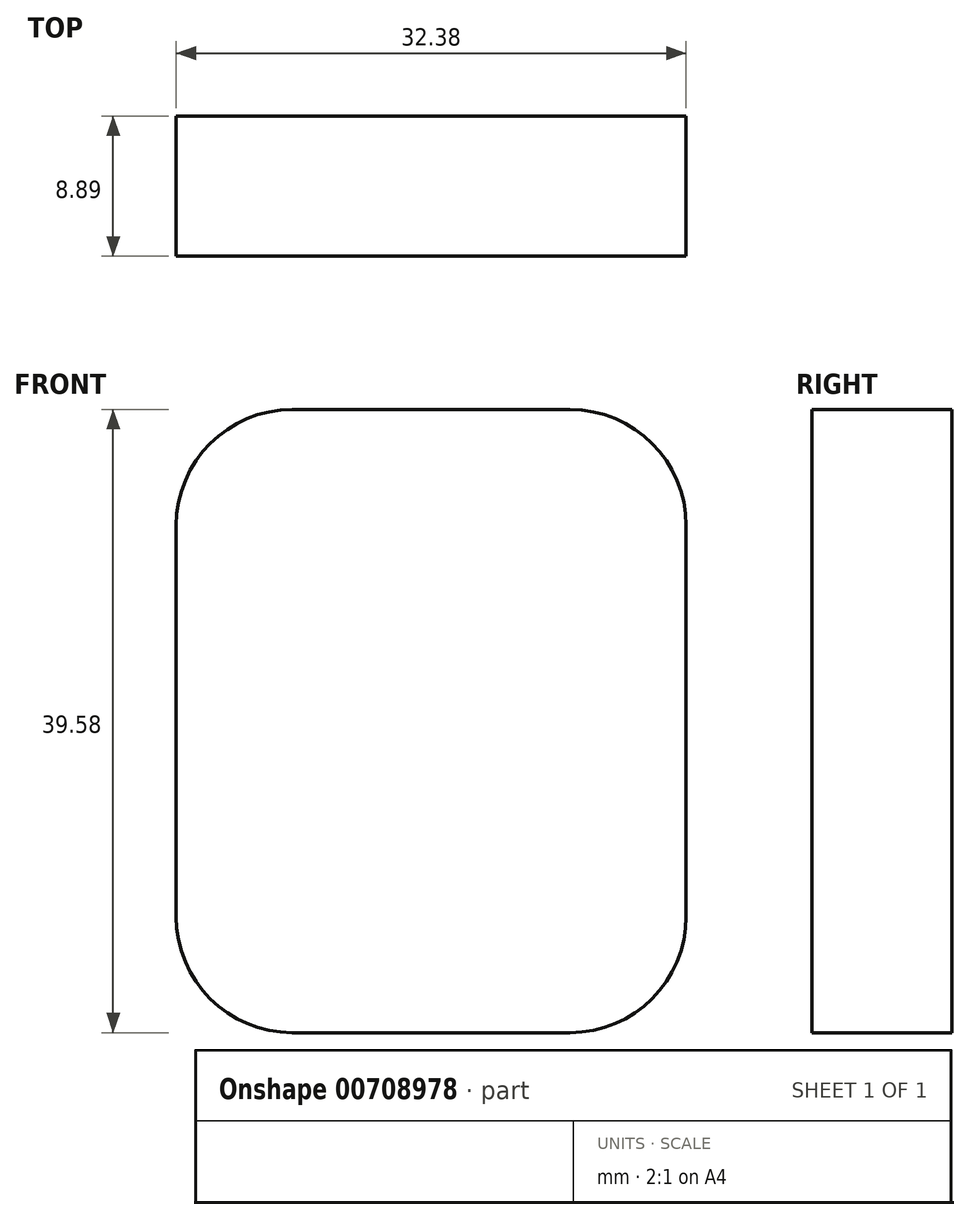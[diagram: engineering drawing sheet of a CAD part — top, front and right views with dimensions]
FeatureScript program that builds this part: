
annotation { "Feature Type Name" : "Feature", "Feature Type Description" : "" }
export const myFeature = defineFeature(function(context is Context, id is Id, definition is map)
    precondition{}
    {
        {
            var Q0;
            Q0=qCreatedBy(makeId("Front.planeOp"),FACE);
            var sketch = newSketch(context, id + "F0", { "sketchPlane" : qUnion([Q0])});
            skLineSegment(sketch, "E0.bottom", {"start": v(8.83, -19.8) * mm, "end": v(-8.83, -19.8) * mm});
            skLineSegment(sketch, "E0.top", {"start": v(8.83, 19.8) * mm, "end": v(-8.83, 19.8) * mm});
            skLineSegment(sketch, "E0.left", {"start": v(16.2, -12.42) * mm, "end": v(16.2, 12.42) * mm});
            skLineSegment(sketch, "E0.right", {"start": v(-16.2, -12.42) * mm, "end": v(-16.2, 12.42) * mm});
            skPoint(sketch, "E0.middle", {"position": v(0, 0) * mm});
            skPoint(sketch, "E1.visualSharp", {"position": v(-16.2, 19.8) * mm});
            skArc(sketch, "E1.filletArc", {"start": v(-8.83, 19.8) * mm, "mid": v(-14.03, 17.63) * mm, "end": v(-16.2, 12.42) * mm});
            skPoint(sketch, "E2.visualSharp", {"position": v(16.2, 19.8) * mm});
            skArc(sketch, "E2.filletArc", {"start": v(16.2, 12.42) * mm, "mid": v(14.03, 17.63) * mm, "end": v(8.83, 19.8) * mm});
            skPoint(sketch, "E3.visualSharp", {"position": v(-16.2, -19.8) * mm});
            skArc(sketch, "E3.filletArc", {"start": v(-16.2, -12.42) * mm, "mid": v(-14.03, -17.63) * mm, "end": v(-8.83, -19.8) * mm});
            skPoint(sketch, "E4.visualSharp", {"position": v(16.2, -19.8) * mm});
            skArc(sketch, "E4.filletArc", {"start": v(8.83, -19.8) * mm, "mid": v(14.03, -17.63) * mm, "end": v(16.2, -12.42) * mm});
            skSolve(sketch);
        }
        {
            var Q0;
            Q0=qSketchRegion(id+"F0",true);
            extrude(context, id + "F1", {"entities" : qUnion([Q0]), "depth" : 8.9 * mm, "offsetDistance" : 25.4 * mm});
        }
    });
